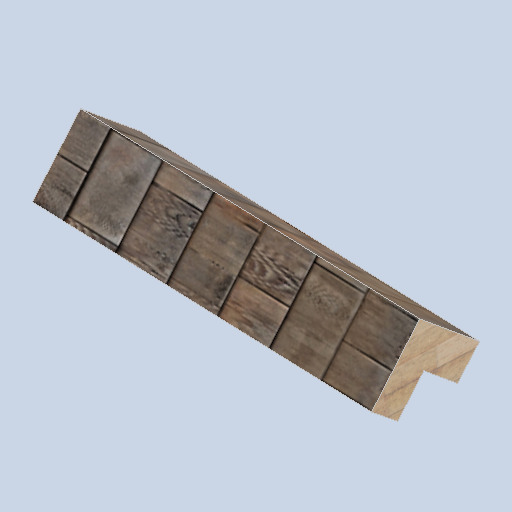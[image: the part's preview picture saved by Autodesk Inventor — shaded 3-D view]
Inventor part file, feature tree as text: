
AUTODESK INVENTOR PART (.ipt)
format: ipt  version: 2024.2 (Build 282272000, 272)  size: 241,664 bytes
history: native  units: in
note: dims shown in document units (in); Inventor stores cm internally (conversion verified against a paired STEP export)
features: sketch x8, plane x5, other x3
ambient origin geometry x8: Origin, YZ Plane, XZ Plane, XY Plane, X Axis, Y Axis, Z Axis, Center Point
bodies: Solid1 (feature_tree)
feature tree (16):
  other  "panel_pad_frame_02.ipt"
  other  "Solid1::panel_pad_frame_02.ipt"
  other  "TaggingFeature1"
  sketch  "Sketch1"  dims[d0=0.3937in]
  sketch  "Sketch2"
  sketch  "Sketch3"
  sketch  "Sketch6"
  sketch  "Sketch7"
  sketch  "Sketch8"
  sketch  "Sketch9"
  sketch  "Sketch10"
  plane  "Work Plane1"
  plane  "Work Plane2"
  plane  "Work Plane3"
  plane  "Work Plane4"
  plane  "Work Plane5"
